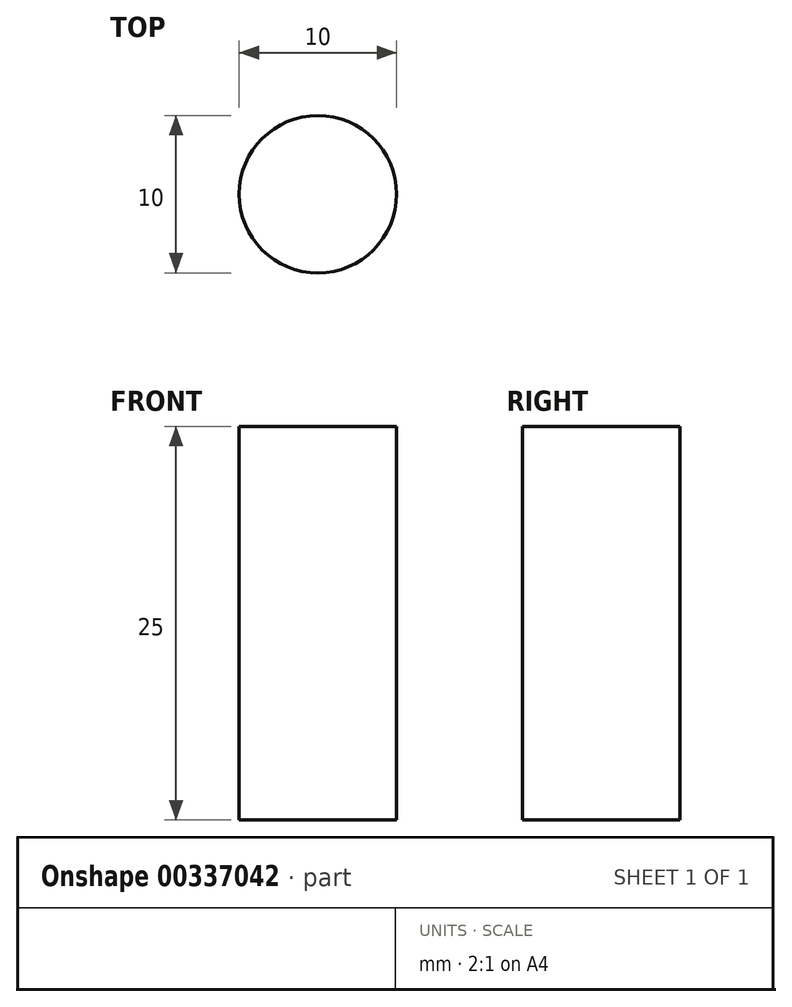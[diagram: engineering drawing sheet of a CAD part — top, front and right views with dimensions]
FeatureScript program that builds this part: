
annotation { "Feature Type Name" : "Feature", "Feature Type Description" : "" }
export const myFeature = defineFeature(function(context is Context, id is Id, definition is map)
    precondition{}
    {
        {
            var Q0;
            Q0=qCreatedBy(makeId("Top.planeOp"),FACE);
            var sketch = newSketch(context, id + "F0", { "sketchPlane" : qUnion([Q0])});
            skCircle(sketch, "E0", {"center": v(0, 0) * mm, "radius": 5 * mm});
            skSolve(sketch);
        }
        {
            var Q0;
            Q0=makeQuery(id+"F0.imprint","IMPRINT",FACE,{"disambiguationData":[TD([[makeQuery(id+"F0.imprint","IMPRINT",EDGE,{"derivedFrom":sQuery(id+"F0.wireOp",EDGE,"E0")}),1.0]])]});
            extrude(context, id + "F1", {"entities" : qUnion([Q0]), "depth" : 25 * mm});
        }
    });
